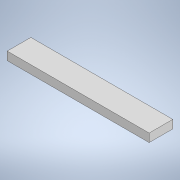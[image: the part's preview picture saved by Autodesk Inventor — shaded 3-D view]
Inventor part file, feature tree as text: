
AUTODESK INVENTOR PART (.ipt)
format: ipt  version: 2022 (Build 260153000, 153)  size: 91,648 bytes
history: native  units: mm
features: extrude x1, sketch x1
ambient origin geometry x8: Origin, YZ Plane, XZ Plane, XY Plane, X Axis, Y Axis, Z Axis, Center Point
bodies: Solid1 (feature_tree)
feature tree (2):
  extrude  "Extrusion1"  Depth=90.0mm
  sketch  "Sketch1"  dims[d0=540.0mm d1=90.0mm d2=31.5mm d3=0.0mm]
